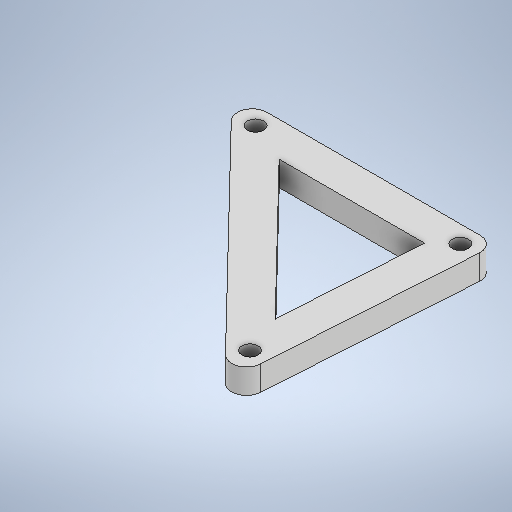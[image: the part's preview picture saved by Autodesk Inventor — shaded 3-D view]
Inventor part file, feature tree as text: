
AUTODESK INVENTOR PART (.ipt)
format: ipt  version: 2025.1 (Build 291241020, 241B)  size: 286,208 bytes
history: native  units: mm
features: extrude x3, sketch x3, fillet x1
ambient origin geometry x8: Origin, YZ Plane, XZ Plane, XY Plane, X Axis, Y Axis, Z Axis, Center Point
bodies: Solid1 (feature_tree)
feature tree (7):
  extrude  "Extrusion1"  Depth=41.5mm
  extrude  "Extrusion2"  Depth=7.0mm
  extrude  "Extrusion3"  Depth=7.0mm
  fillet  "Fillet1"  Radius=3.3mm
  sketch  "Sketch1"  dims[d0=41.5mm d1=55.8mm]
  sketch  "Sketch2"  dims[d2=7.996575mm d3=7.0mm]
  sketch  "Sketch3"  dims[d4=7.0mm d5=7.0mm d6=3.3mm d7=3.3mm d8=3.3mm d9=5.0mm d10=0.0mm d11=23.418828mm d12=10.0mm d13=0.0mm d14=5.0mm d15=0.0mm d16=3.0mm]
